# Revit family: ERA_LF_CS_SPO-6-36
name_source: partatom
category: Осветительные приборы
units: mm (PartAtom-declared; Revit-internal decimal feet)

## family parameters
Всегда вертикально = Да
Заголовок OmniClass = Lighting
Источник света = Да
На основе рабочей плоскости = Нет
Номер OmniClass = 23.80.70.00
Общий = Нет
При загрузке вырезать с полостями = Нет
Размер круглого соединителя = Использовать диаметр
Тип детали = Нормальный
Точка расчета площади = Да

## types (18) — shared parameters
ADSK_Единица измерения = шт.
ADSK_Завод-изготовитель = ЭРА
ADSK_Классификация нагрузок = Освещение
ADSK_Количество фаз = 1
ADSK_Коэффициент мощности = 0.9
ADSK_Наименование краткое = Светильник
ADSK_Напряжение = 230 В
ADSK_Примечание = Импульсный драйвер, поликарбонат
URL = https://www.eraworld.ru
_Корпус_Диаметр = 1 мм
Видимая форма излучения при визуализации = Нет
Источник света = LED
Класс защиты = I
Класс пожароопасности = Нет
Комплект = Импульсный драйвер, поликарбонат
Разработчик модели = https://www.teslabim.ru
Светофильтр = 16777215
Смещение цветовой температуры при затухании лампы = <Нет>
Степень защиты IP = IP40
Тип установки = Потолочный
УГО_Масштаб = 100
Угол наклона = 90,00°
Файл фотометрической сетки = SPO-6-36-4K-M.ies
Цвет = Белый
zero-valued in all types: ADSK_Размер_Диаметр

## per-type parameters (varying)
| type | ADSK_Марка | ADSK_Масса | ADSK_Наименование | ADSK_Номинальная мощность | ADSK_Обозначение | ADSK_Полная мощность | ADSK_Размер_Высота | ADSK_Размер_Длина | ADSK_Размер_Ширина | _Корпус_Высота | _Корпус_Длина | _Корпус_Ширина | _УГО_Диаметр | _УГО_Длина | _УГО_Ширина | Геометрия изделия | Излучение по длине прямоугольника | Излучение по ширине прямоугольника |
| SPO-6-36-6K-P, LED, IP40, 595х595х19 мм (ДхШхВ), 36 Вт, 6500 К, 3060 лм, класс защиты I, в комплекте (импульсный драйвер, поликарбонат) | SPO-6-36-6K-P | 1.28 | Светильник, LED, квадратный, потолочный, IP40, 595х595х19 мм (ДхШхВ), 36 Вт, 6500 К, 3060 лм, класс защиты I, в комплекте (импульсный драйвер, поликарбонат) | 36 Вт | SPO-6-36-6K-P | 40 В·А | 19 мм | 595 мм | 595 мм | 19 мм | 595 мм | 595 мм | 5.95 мм | 5.95 мм | 5.95 мм | Квадратный | 595 мм | 595 мм |
| SPO-6-36-4K-P, LED, IP40, 595х595х19 мм (ДхШхВ), 36 Вт, 4000 К, 3060 лм, класс защиты I, в комплекте (импульсный драйвер, поликарбонат) | SPO-6-36-4K-P | 1.18 | Светильник, LED, квадратный, потолочный, IP40, 595х595х19 мм (ДхШхВ), 36 Вт, 4000 К, 3060 лм, класс защиты I, в комплекте (импульсный драйвер, поликарбонат) | 36 Вт | SPO-6-36-4K-P | 40 В·А | 19 мм | 595 мм | 595 мм | 19 мм | 595 мм | 595 мм | 5.95 мм | 5.95 мм | 5.95 мм | Квадратный | 595 мм | 595 мм |
| SPO-6-36-6K-M, LED, IP40, 595х595х19 мм (ДхШхВ), 36 Вт, 6500 К, 3060 лм, класс защиты I, в комплекте (импульсный драйвер, поликарбонат) | SPO-6-36-6K-M | 1.18 | Светильник, LED, квадратный, потолочный, IP40, 595х595х19 мм (ДхШхВ), 36 Вт, 6500 К, 3060 лм, класс защиты I, в комплекте (импульсный драйвер, поликарбонат) | 36 Вт | SPO-6-36-6K-M | 40 В·А | 19 мм | 595 мм | 595 мм | 19 мм | 595 мм | 595 мм | 5.95 мм | 5.95 мм | 5.95 мм | Квадратный | 595 мм | 595 мм |
| SPO-6-36-4K-M, LED, IP40, 595х595х19 мм (ДхШхВ), 36 Вт, 4000 К, 3060 лм, класс защиты I, в комплекте (импульсный драйвер, поликарбонат) | SPO-6-36-4K-M | 1.2 | Светильник, LED, квадратный, потолочный, IP40, 595х595х19 мм (ДхШхВ), 36 Вт, 4000 К, 3060 лм, класс защиты I, в комплекте (импульсный драйвер, поликарбонат) | 36 Вт | SPO-6-36-4K-M | 40 В·А | 19 мм | 595 мм | 595 мм | 19 мм | 595 мм | 595 мм | 5.95 мм | 5.95 мм | 5.95 мм | Квадратный | 595 мм | 595 мм |
| SPO-6-48-6K-P, LED, IP40, 595х595х19 мм (ДхШхВ), 48 Вт, 6500 К, 4200 лм, класс защиты I, в комплекте (импульсный драйвер, поликарбонат) | SPO-6-48-6K-P | 1.3 | Светильник, LED, квадратный, потолочный, IP40, 595х595х19 мм (ДхШхВ), 48 Вт, 6500 К, 4200 лм, класс защиты I, в комплекте (импульсный драйвер, поликарбонат) | 48 Вт | SPO-6-48-6K-P | 53 В·А | 19 мм | 595 мм | 595 мм | 19 мм | 595 мм | 595 мм | 5.95 мм | 5.95 мм | 5.95 мм | Квадратный | 595 мм | 595 мм |
| SPO-6-48-4K-P, LED, IP40, 595х595х19 мм (ДхШхВ), 48 Вт, 4000 К, 4200 лм, класс защиты I, в комплекте (импульсный драйвер, поликарбонат) | SPO-6-48-4K-P | 1.24 | Светильник, LED, квадратный, потолочный, IP40, 595х595х19 мм (ДхШхВ), 48 Вт, 4000 К, 4200 лм, класс защиты I, в комплекте (импульсный драйвер, поликарбонат) | 48 Вт | SPO-6-48-4K-P | 53 В·А | 19 мм | 595 мм | 595 мм | 19 мм | 595 мм | 595 мм | 5.95 мм | 5.95 мм | 5.95 мм | Квадратный | 595 мм | 595 мм |
| SPO-6-48-6K-M, LED, IP40, 595х595х19 мм (ДхШхВ), 48 Вт, 6500 К, 4200 лм, класс защиты I, в комплекте (импульсный драйвер, поликарбонат) | SPO-6-48-6K-M | 1.36 | Светильник, LED, квадратный, потолочный, IP40, 595х595х19 мм (ДхШхВ), 48 Вт, 6500 К, 4200 лм, класс защиты I, в комплекте (импульсный драйвер, поликарбонат) | 48 Вт | SPO-6-48-6K-M | 53 В·А | 19 мм | 595 мм | 595 мм | 19 мм | 595 мм | 595 мм | 5.95 мм | 5.95 мм | 5.95 мм | Квадратный | 595 мм | 595 мм |
| SPO-6-48-4K-M, LED, IP40, 595х595х19 мм (ДхШхВ), 48 Вт, 4000 К, 4200 лм, класс защиты I, в комплекте (импульсный драйвер, поликарбонат) | SPO-6-48-4K-M | 1.34 | Светильник, LED, квадратный, потолочный, IP40, 595х595х19 мм (ДхШхВ), 48 Вт, 4000 К, 4200 лм, класс защиты I, в комплекте (импульсный драйвер, поликарбонат) | 48 Вт | SPO-6-48-4K-M | 53 В·А | 19 мм | 595 мм | 595 мм | 19 мм | 595 мм | 595 мм | 5.95 мм | 5.95 мм | 5.95 мм | Квадратный | 595 мм | 595 мм |
| SPO-6-72-6K-P, LED, IP40, 595х595х19 мм (ДхШхВ), 72 Вт, 6500 К, 6120 лм, класс защиты I, в комплекте (импульсный драйвер, поликарбонат) | SPO-6-72-6K-P | 1.42 | Светильник, LED, квадратный, потолочный, IP40, 595х595х19 мм (ДхШхВ), 72 Вт, 6500 К, 6120 лм, класс защиты I, в комплекте (импульсный драйвер, поликарбонат) | 72 Вт | SPO-6-72-6K-P | 80 В·А | 19 мм | 595 мм | 595 мм | 19 мм | 595 мм | 595 мм | 5.95 мм | 5.95 мм | 5.95 мм | Квадратный | 595 мм | 595 мм |
| SPO-6-72-4K-P, LED, IP40, 595х595х19 мм (ДхШхВ), 72 Вт, 4000 К, 6120 лм, класс защиты I, в комплекте (импульсный драйвер, поликарбонат) | SPO-6-72-4K-P | 1.4 | Светильник, LED, квадратный, потолочный, IP40, 595х595х19 мм (ДхШхВ), 72 Вт, 4000 К, 6120 лм, класс защиты I, в комплекте (импульсный драйвер, поликарбонат) | 72 Вт | SPO-6-72-4K-P | 80 В·А | 19 мм | 595 мм | 595 мм | 19 мм | 595 мм | 595 мм | 5.95 мм | 5.95 мм | 5.95 мм | Квадратный | 595 мм | 595 мм |
| SPO-1-40-6K-M, LED, IP40, 595х595х25 мм (ДхШхВ), 40 Вт, 6500 К, 3060 лм, класс защиты I, в комплекте (импульсный драйвер, поликарбонат) | SPO-1-40-6K-M | 1.26 | Светильник, LED, квадратный, потолочный, IP40, 595х595х25 мм (ДхШхВ), 40 Вт, 6500 К, 3060 лм, класс защиты I, в комплекте (импульсный драйвер, поликарбонат) | 40 Вт | SPO-1-40-6K-M | 44 В·А | 25 мм | 595 мм | 595 мм | 25 мм | 595 мм | 595 мм | 5.95 мм | 5.95 мм | 5.95 мм | Квадратный | 595 мм | 595 мм |
| SPO-1-40-4K-M, LED, IP40, 595х595х25 мм (ДхШхВ), 40 Вт, 4000 К, 3060 лм, класс защиты I, в комплекте (импульсный драйвер, поликарбонат) | SPO-1-40-4K-M | 1.26 | Светильник, LED, квадратный, потолочный, IP40, 595х595х25 мм (ДхШхВ), 40 Вт, 4000 К, 3060 лм, класс защиты I, в комплекте (импульсный драйвер, поликарбонат) | 40 Вт | SPO-1-40-4K-M | 44 В·А | 25 мм | 595 мм | 595 мм | 25 мм | 595 мм | 595 мм | 5.95 мм | 5.95 мм | 5.95 мм | Квадратный | 595 мм | 595 мм |
| SPO-7-40-6K-P, LED, IP40, 1200х180х19 мм (ДхШхВ), 40 Вт, 6500 К, 2800 лм, класс защиты I, в комплекте (импульсный драйвер, поликарбонат) | SPO-7-40-6K-P | 1.08 | Светильник, LED, прямоугольный, потолочный, IP40, 1200х180х19 мм (ДхШхВ), 40 Вт, 6500 К, 2800 лм, класс защиты I, в комплекте (импульсный драйвер, поликарбонат) | 40 Вт | SPO-7-40-6K-P | 44 В·А | 19 мм | 1200 мм | 180 мм | 19 мм | 1200 мм | 180 мм | 12 мм | 12 мм | 1.8 мм | Прямоугольный | 1200 мм | 180 мм |
| SPO-7-40-4K-P, LED, IP40, 1200х180х19 мм (ДхШхВ), 40 Вт, 4000 К, 2800 лм, класс защиты I, в комплекте (импульсный драйвер, поликарбонат) | SPO-7-40-4K-P | 1.08 | Светильник, LED, прямоугольный, потолочный, IP40, 1200х180х19 мм (ДхШхВ), 40 Вт, 4000 К, 2800 лм, класс защиты I, в комплекте (импульсный драйвер, поликарбонат) | 40 Вт | SPO-7-40-4K-P | 44 В·А | 19 мм | 1200 мм | 180 мм | 19 мм | 1200 мм | 180 мм | 12 мм | 12 мм | 1.8 мм | Прямоугольный | 1200 мм | 180 мм |
| SPO-7-40-6K-M, LED, IP40, 1200х180х19 мм (ДхШхВ), 40 Вт, 6500 К, 2800 лм, класс защиты I, в комплекте (импульсный драйвер, поликарбонат) | SPO-7-40-6K-M | 1.1 | Светильник, LED, прямоугольный, потолочный, IP40, 1200х180х19 мм (ДхШхВ), 40 Вт, 6500 К, 2800 лм, класс защиты I, в комплекте (импульсный драйвер, поликарбонат) | 40 Вт | SPO-7-40-6K-M | 44 В·А | 19 мм | 1200 мм | 180 мм | 19 мм | 1200 мм | 180 мм | 12 мм | 12 мм | 1.8 мм | Прямоугольный | 1200 мм | 180 мм |
| SPO-7-40-4K-M, LED, IP40, 1200х180х19 мм (ДхШхВ), 40 Вт, 4000 К, 2800 лм, класс защиты I, в комплекте (импульсный драйвер, поликарбонат) | SPO-7-40-4K-M | 1.08 | Светильник, LED, прямоугольный, потолочный, IP40, 1200х180х19 мм (ДхШхВ), 40 Вт, 4000 К, 2800 лм, класс защиты I, в комплекте (импульсный драйвер, поликарбонат) | 40 Вт | SPO-7-40-4K-M | 44 В·А | 19 мм | 1200 мм | 180 мм | 19 мм | 1200 мм | 180 мм | 12 мм | 12 мм | 1.8 мм | Прямоугольный | 1200 мм | 180 мм |
| SPO-7-72-6K-P, LED, IP40, 1200х180х19 мм (ДхШхВ), 72 Вт, 6500 К, 5000 лм, класс защиты I, в комплекте (импульсный драйвер, поликарбонат) | SPO-7-72-6K-P | 1.28 | Светильник, LED, прямоугольный, потолочный, IP40, 1200х180х19 мм (ДхШхВ), 72 Вт, 6500 К, 5000 лм, класс защиты I, в комплекте (импульсный драйвер, поликарбонат) | 72 Вт | SPO-7-72-6K-P | 80 В·А | 19 мм | 1200 мм | 180 мм | 19 мм | 1200 мм | 180 мм | 12 мм | 12 мм | 1.8 мм | Прямоугольный | 1200 мм | 180 мм |
| SPO-7-72-4K-P, LED, IP40, 1200х180х19 мм (ДхШхВ), 72 Вт, 4000 К, 5000 лм, класс защиты I, в комплекте (импульсный драйвер, поликарбонат) | SPO-7-72-4K-P | 1.32 | Светильник, LED, прямоугольный, потолочный, IP40, 1200х180х19 мм (ДхШхВ), 72 Вт, 4000 К, 5000 лм, класс защиты I, в комплекте (импульсный драйвер, поликарбонат) | 72 Вт | SPO-7-72-4K-P | 80 В·А | 19 мм | 1200 мм | 180 мм | 19 мм | 1200 мм | 180 мм | 12 мм | 12 мм | 1.8 мм | Прямоугольный | 1200 мм | 180 мм |
